# Revit family: Thorn RACE Bollard
name_source: partatom
category: Lighting Fixtures
revit_build: Autodesk Revit 2016 (Build: 20150220_1215(x64)
units: mm (PartAtom-declared; Revit-internal decimal feet)

## family parameters
Always vertical = Yes
Cut with Voids When Loaded = No
Light Source = Yes
OmniClass Number = 23.80.70.14
OmniClass Title = Luminaries for External Lighting
Part Type = Normal
Room Calculation Point = No
Round Connector Dimension = Use Diameter
Shared = No
Work Plane-Based = No

## types (3) — shared parameters
Assembly Code = D5020200
Body = Thorn_Metal_Dark_Grey
Color Filter = 16777215
Cover = Thorn_Cover_Self_llumination
Description = LED bollard
Dimming Lamp Color Temperature Shift = <None>
Length = 173 mm  [stored 0.567585 ft]
Manufacturer = Thorn Lighting
Metal = Thorn_Metal_Grey
Tilt Angle = 90.00°
Voltage = 230 V
Width = 220 mm  [stored 0.721785 ft]

## per-type parameters (varying)
| type | Apparent Load | Height | Model | Photometric Web File | URL |
| RAB 400mm | 9 VA | 400 mm  [stored 1.31234 ft] | 96632074 | TL_RAB1L20WP830.IES | www.thornlighting.com/96632074 |
| RAB 700mm | 15 VA | 700 mm  [stored 2.29659 ft] | 96632076 | TL_RAB1L35WPC830.IES | www.thornlighting.com/96632076 |
| RAB 900mm | 9 VA | 900 mm  [stored 2.95276 ft] | 96632082 | TL_RAB1L20WPC830.IES | www.thornlighting.com/96632082 |

note: [stored X ft] marks values corroborated as IEEE doubles in the binary element streams (Revit-internal decimal feet)

## geometry (parser evidence)
native form markers: Sweep x5
no freeform markers — native parametric forms only
